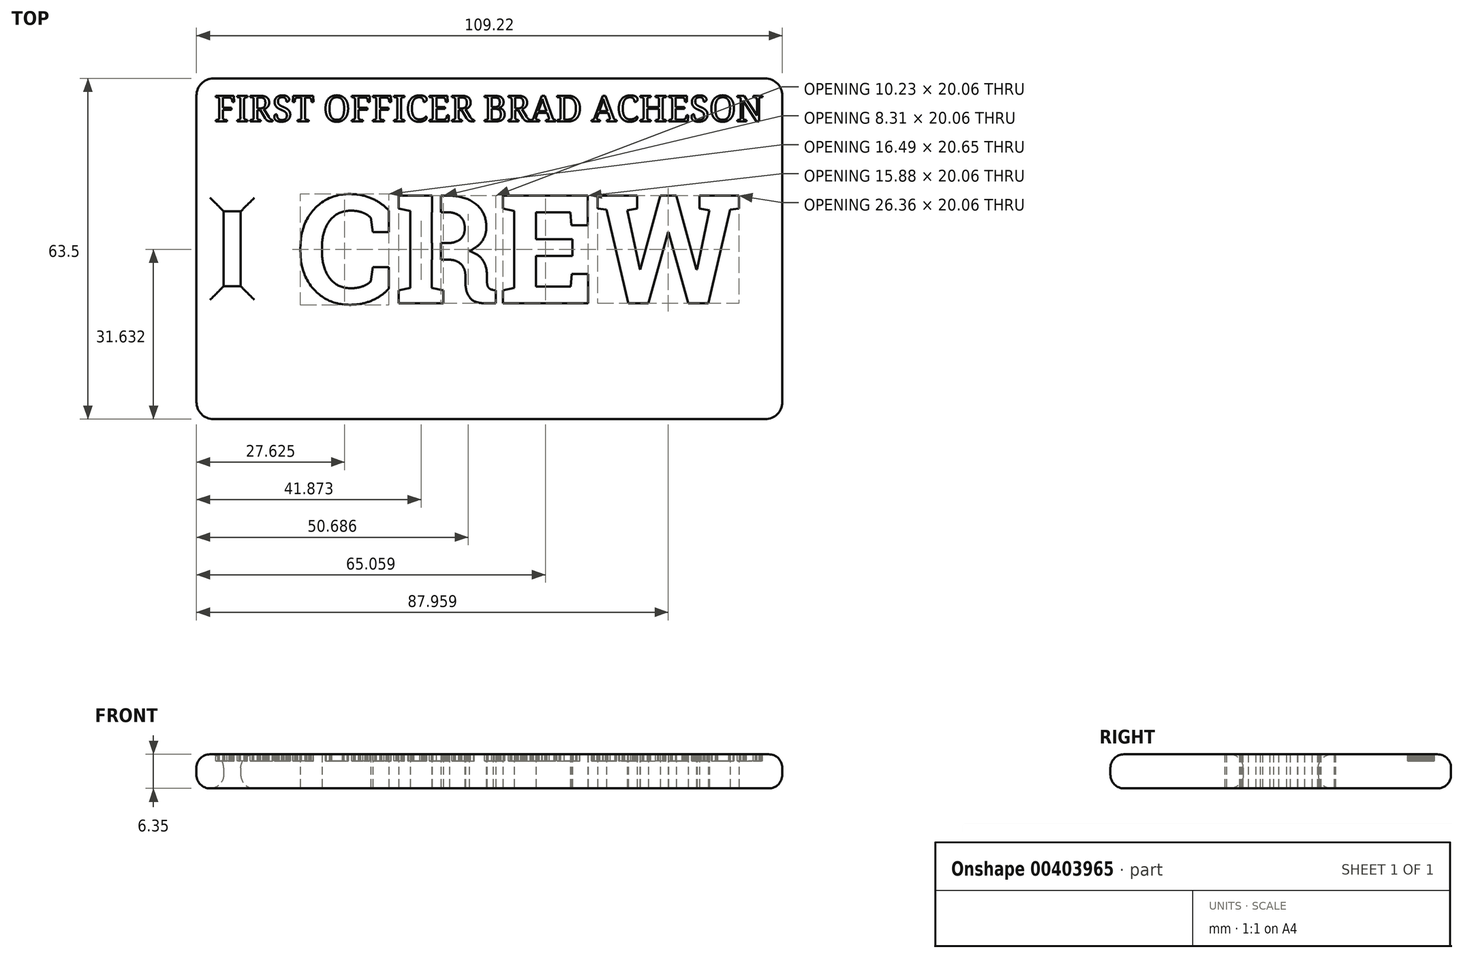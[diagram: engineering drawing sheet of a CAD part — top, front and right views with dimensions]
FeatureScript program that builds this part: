
annotation { "Feature Type Name" : "Feature", "Feature Type Description" : "" }
export const myFeature = defineFeature(function(context is Context, id is Id, definition is map)
    precondition{}
    {
        {
            var Q0;
            Q0=qCreatedBy(makeId("Top.planeOp"),FACE);
            var sketch = newSketch(context, id + "F0", { "sketchPlane" : qUnion([Q0])});
            skLineSegment(sketch, "E0.bottom", {"start": v(3.18, 0) * mm, "end": v(106.05, 0) * mm});
            skLineSegment(sketch, "E0.top", {"start": v(3.18, -63.5) * mm, "end": v(106.05, -63.5) * mm});
            skLineSegment(sketch, "E0.left", {"start": v(0, -3.18) * mm, "end": v(0, -60.33) * mm});
            skLineSegment(sketch, "E0.right", {"start": v(109.22, -3.18) * mm, "end": v(109.22, -60.33) * mm});
            skLineSegment(sketch, "E1.bottom", {"start": v(5.08, -24.77) * mm, "end": v(8.25, -24.77) * mm});
            skLineSegment(sketch, "E1.top", {"start": v(5.08, -38.74) * mm, "end": v(8.25, -38.74) * mm});
            skLineSegment(sketch, "E1.left", {"start": v(5.08, -24.76) * mm, "end": v(5.08, -38.73) * mm});
            skLineSegment(sketch, "E1.right", {"start": v(8.25, -24.76) * mm, "end": v(8.25, -38.73) * mm});
            skLineSegment(sketch, "E2", {"start": v(0, -31.75) * mm, "end": v(109.22, -31.75) * mm, "construction": true});
            skPoint(sketch, "E3.visualSharp", {"position": v(0, 0) * mm});
            skArc(sketch, "E3.filletArc", {"start": v(3.17, 0) * mm, "mid": v(0.93, -0.93) * mm, "end": v(0, -3.18) * mm});
            skPoint(sketch, "E4.visualSharp", {"position": v(109.22, 0) * mm});
            skArc(sketch, "E4.filletArc", {"start": v(109.22, -3.18) * mm, "mid": v(108.3, -0.93) * mm, "end": v(106.05, 0) * mm});
            skPoint(sketch, "E5.visualSharp", {"position": v(109.22, -63.5) * mm});
            skArc(sketch, "E5.filletArc", {"start": v(106.05, -63.5) * mm, "mid": v(108.3, -62.57) * mm, "end": v(109.22, -60.33) * mm});
            skPoint(sketch, "E6.visualSharp", {"position": v(0, -63.5) * mm});
            skArc(sketch, "E6.filletArc", {"start": v(0, -60.33) * mm, "mid": v(0.93, -62.57) * mm, "end": v(3.18, -63.5) * mm});
            skText(sketch, "E7", { "text": "CREW", "fontName": "RobotoSlab-Bold.ttf"});
            skLineSegment(sketch, "E8.bottom", {"start": v(45.57, -26.63) * mm, "end": v(43.9, -26.63) * mm});
            skLineSegment(sketch, "E8.top", {"start": v(45.57, -20.7) * mm, "end": v(43.9, -20.7) * mm});
            skLineSegment(sketch, "E8.left", {"start": v(45.57, -26.63) * mm, "end": v(45.57, -20.7) * mm});
            skLineSegment(sketch, "E8.right", {"start": v(43.9, -26.63) * mm, "end": v(43.9, -20.7) * mm});
            skLineSegment(sketch, "E9.bottom", {"start": v(45.57, -34.32) * mm, "end": v(43.9, -34.32) * mm});
            skLineSegment(sketch, "E9.top", {"start": v(45.57, -30.21) * mm, "end": v(43.9, -30.21) * mm});
            skLineSegment(sketch, "E9.left", {"start": v(45.57, -34.32) * mm, "end": v(45.57, -30.21) * mm});
            skLineSegment(sketch, "E9.right", {"start": v(43.9, -34.32) * mm, "end": v(43.9, -30.21) * mm});
            skLineSegment(sketch, "E10", {"start": v(43.9, -26.63) * mm, "end": v(43.9, -30.21) * mm, "construction": true});
            skLineSegment(sketch, "E11", {"start": v(45.57, -26.63) * mm, "end": v(45.57, -30.21) * mm, "construction": true});
            const initialGuessF0  = {"E7": [0.01866, -0.0419, 1, 0, 0.02032]};
            skSetInitialGuess(sketch, initialGuessF0);
            skSolve(sketch);
        }
        {
            var Q0;
            Q0=makeQuery(id+"F0.imprint","IMPRINT",FACE,{"disambiguationData":[TD([[makeQuery(id+"F0.imprint","IMPRINT",EDGE,{"derivedFrom":sQuery(id+"F0.wireOp",EDGE,"E0.bottom")}),-1.0]])]});
            var Q1;
            {var subQ0=sQuery(id+"F0.wireOp",EDGE,"E8.right");var subQ1=sQuery(id+"F0.wireOp",EDGE,"E7.sketch_text.stroke-52");var subQ2=makeQuery(id+"F0.imprint","INTERSECT",VERTEX,{"derivedFrom":[subQ1,subQ0]});Q1=makeQuery(id+"F0.imprint","IMPRINT",FACE,{"disambiguationData":[TD([[makeQuery(id+"F0.imprint","IMPRINT",EDGE,{"disambiguationData":[TD([[subQ2,-1.0]])],"derivedFrom":subQ1}),-1.0]])]});}
            var Q2;
            {var subQ5=sQuery(id+"F0.wireOp",EDGE,"E8.top");Q2=makeQuery(id+"F0.imprint","IMPRINT",FACE,{"disambiguationData":[TD([[makeQuery(id+"F0.imprint","IMPRINT",EDGE,{"derivedFrom":subQ5}),1.0]])]});}
            var Q3;
            {var subQ12=sQuery(id+"F0.wireOp",EDGE,"E7.sketch_text.stroke-54");Q3=makeQuery(id+"F0.imprint","IMPRINT",FACE,{"disambiguationData":[TD([[makeQuery(id+"F0.imprint","IMPRINT",EDGE,{"derivedFrom":subQ12}),1.0]])]});}
            var Q4;
            {var subQ5=sQuery(id+"F0.wireOp",EDGE,"E8.bottom");Q4=makeQuery(id+"F0.imprint","IMPRINT",FACE,{"disambiguationData":[TD([[makeQuery(id+"F0.imprint","IMPRINT",EDGE,{"derivedFrom":subQ5}),-1.0]])]});}
            var Q5;
            {var subQ5=sQuery(id+"F0.wireOp",EDGE,"E9.top");Q5=makeQuery(id+"F0.imprint","IMPRINT",FACE,{"disambiguationData":[TD([[makeQuery(id+"F0.imprint","IMPRINT",EDGE,{"derivedFrom":subQ5}),1.0]])]});}
            var Q6;
            {var subQ5=sQuery(id+"F0.wireOp",EDGE,"E9.bottom");Q6=makeQuery(id+"F0.imprint","IMPRINT",FACE,{"disambiguationData":[TD([[makeQuery(id+"F0.imprint","IMPRINT",EDGE,{"derivedFrom":subQ5}),-1.0]])]});}
            var Q7;
            {var subQ0=sQuery(id+"F0.wireOp",EDGE,"E9.left");var subQ1=sQuery(id+"F0.wireOp",EDGE,"E7.sketch_text.stroke-41");var subQ2=makeQuery(id+"F0.imprint","INTERSECT",VERTEX,{"derivedFrom":[subQ1,subQ0]});Q7=makeQuery(id+"F0.imprint","IMPRINT",FACE,{"disambiguationData":[TD([[makeQuery(id+"F0.imprint","IMPRINT",EDGE,{"disambiguationData":[TD([[subQ2,-1.0]])],"derivedFrom":subQ1}),-1.0]])]});}
            extrude(context, id + "F1", {"entities" : qUnion([Q0, Q1, Q2, Q3, Q4, Q5, Q6, Q7]), "depth" : 6.35 * mm});
        }
        {
            var Q0;
            Q0=makeQuery(id+"F1.opExtrude","CAP_FACE",FACE,{"disambiguationData":[OSD([sQuery(id+"F0.wireOp",EDGE,"E0.bottom"),sQuery(id+"F0.wireOp",EDGE,"E0.top"),sQuery(id+"F0.wireOp",EDGE,"E0.left"),sQuery(id+"F0.wireOp",EDGE,"E0.right"),sQuery(id+"F0.wireOp",EDGE,"E1.bottom"),sQuery(id+"F0.wireOp",EDGE,"E1.top"),sQuery(id+"F0.wireOp",EDGE,"E1.left"),sQuery(id+"F0.wireOp",EDGE,"E1.right"),sQuery(id+"F0.wireOp",EDGE,"E3.filletArc"),sQuery(id+"F0.wireOp",EDGE,"E4.filletArc"),sQuery(id+"F0.wireOp",EDGE,"E5.filletArc"),sQuery(id+"F0.wireOp",EDGE,"E6.filletArc"),sQuery(id+"F0.wireOp",EDGE,"E7.sketch_text.stroke-0"),sQuery(id+"F0.wireOp",EDGE,"E7.sketch_text.stroke-1"),sQuery(id+"F0.wireOp",EDGE,"E7.sketch_text.stroke-2"),sQuery(id+"F0.wireOp",EDGE,"E7.sketch_text.stroke-3"),sQuery(id+"F0.wireOp",EDGE,"E7.sketch_text.stroke-4"),sQuery(id+"F0.wireOp",EDGE,"E7.sketch_text.stroke-5"),sQuery(id+"F0.wireOp",EDGE,"E7.sketch_text.stroke-6"),sQuery(id+"F0.wireOp",EDGE,"E7.sketch_text.stroke-7"),sQuery(id+"F0.wireOp",EDGE,"E7.sketch_text.stroke-8"),sQuery(id+"F0.wireOp",EDGE,"E7.sketch_text.stroke-9"),sQuery(id+"F0.wireOp",EDGE,"E7.sketch_text.stroke-10"),sQuery(id+"F0.wireOp",EDGE,"E7.sketch_text.stroke-11"),sQuery(id+"F0.wireOp",EDGE,"E7.sketch_text.stroke-12"),sQuery(id+"F0.wireOp",EDGE,"E7.sketch_text.stroke-13"),sQuery(id+"F0.wireOp",EDGE,"E7.sketch_text.stroke-14"),sQuery(id+"F0.wireOp",EDGE,"E7.sketch_text.stroke-15"),sQuery(id+"F0.wireOp",EDGE,"E7.sketch_text.stroke-16"),sQuery(id+"F0.wireOp",EDGE,"E7.sketch_text.stroke-17"),sQuery(id+"F0.wireOp",EDGE,"E7.sketch_text.stroke-18"),sQuery(id+"F0.wireOp",EDGE,"E7.sketch_text.stroke-19"),sQuery(id+"F0.wireOp",EDGE,"E7.sketch_text.stroke-20"),sQuery(id+"F0.wireOp",EDGE,"E7.sketch_text.stroke-21"),sQuery(id+"F0.wireOp",EDGE,"E7.sketch_text.stroke-22"),sQuery(id+"F0.wireOp",EDGE,"E7.sketch_text.stroke-23"),sQuery(id+"F0.wireOp",EDGE,"E7.sketch_text.stroke-24"),sQuery(id+"F0.wireOp",EDGE,"E7.sketch_text.stroke-25"),sQuery(id+"F0.wireOp",EDGE,"E7.sketch_text.stroke-26"),sQuery(id+"F0.wireOp",EDGE,"E7.sketch_text.stroke-27"),sQuery(id+"F0.wireOp",EDGE,"E7.sketch_text.stroke-28"),sQuery(id+"F0.wireOp",EDGE,"E7.sketch_text.stroke-29"),sQuery(id+"F0.wireOp",EDGE,"E7.sketch_text.stroke-30"),sQuery(id+"F0.wireOp",EDGE,"E7.sketch_text.stroke-31"),sQuery(id+"F0.wireOp",EDGE,"E7.sketch_text.stroke-32"),sQuery(id+"F0.wireOp",EDGE,"E7.sketch_text.stroke-33"),sQuery(id+"F0.wireOp",EDGE,"E7.sketch_text.stroke-34"),sQuery(id+"F0.wireOp",EDGE,"E7.sketch_text.stroke-35"),sQuery(id+"F0.wireOp",EDGE,"E7.sketch_text.stroke-36"),sQuery(id+"F0.wireOp",EDGE,"E7.sketch_text.stroke-37"),sQuery(id+"F0.wireOp",EDGE,"E7.sketch_text.stroke-38"),sQuery(id+"F0.wireOp",EDGE,"E7.sketch_text.stroke-39"),sQuery(id+"F0.wireOp",EDGE,"E7.sketch_text.stroke-40"),sQuery(id+"F0.wireOp",EDGE,"E7.sketch_text.stroke-41"),sQuery(id+"F0.wireOp",EDGE,"E7.sketch_text.stroke-42"),sQuery(id+"F0.wireOp",EDGE,"E7.sketch_text.stroke-43"),sQuery(id+"F0.wireOp",EDGE,"E7.sketch_text.stroke-44"),sQuery(id+"F0.wireOp",EDGE,"E7.sketch_text.stroke-45"),sQuery(id+"F0.wireOp",EDGE,"E7.sketch_text.stroke-46"),sQuery(id+"F0.wireOp",EDGE,"E7.sketch_text.stroke-47"),sQuery(id+"F0.wireOp",EDGE,"E7.sketch_text.stroke-48"),sQuery(id+"F0.wireOp",EDGE,"E7.sketch_text.stroke-49"),sQuery(id+"F0.wireOp",EDGE,"E7.sketch_text.stroke-50"),sQuery(id+"F0.wireOp",EDGE,"E7.sketch_text.stroke-51"),sQuery(id+"F0.wireOp",EDGE,"E7.sketch_text.stroke-52"),sQuery(id+"F0.wireOp",EDGE,"E7.sketch_text.stroke-53"),sQuery(id+"F0.wireOp",EDGE,"E7.sketch_text.stroke-54"),sQuery(id+"F0.wireOp",EDGE,"E7.sketch_text.stroke-55"),sQuery(id+"F0.wireOp",EDGE,"E7.sketch_text.stroke-56"),sQuery(id+"F0.wireOp",EDGE,"E7.sketch_text.stroke-57"),sQuery(id+"F0.wireOp",EDGE,"E7.sketch_text.stroke-58"),sQuery(id+"F0.wireOp",EDGE,"E7.sketch_text.stroke-59"),sQuery(id+"F0.wireOp",EDGE,"E7.sketch_text.stroke-60"),sQuery(id+"F0.wireOp",EDGE,"E7.sketch_text.stroke-61"),sQuery(id+"F0.wireOp",EDGE,"E7.sketch_text.stroke-62"),sQuery(id+"F0.wireOp",EDGE,"E7.sketch_text.stroke-63"),sQuery(id+"F0.wireOp",EDGE,"E7.sketch_text.stroke-64"),sQuery(id+"F0.wireOp",EDGE,"E7.sketch_text.stroke-65"),sQuery(id+"F0.wireOp",EDGE,"E7.sketch_text.stroke-66"),sQuery(id+"F0.wireOp",EDGE,"E7.sketch_text.stroke-67"),sQuery(id+"F0.wireOp",EDGE,"E7.sketch_text.stroke-68"),sQuery(id+"F0.wireOp",EDGE,"E7.sketch_text.stroke-69"),sQuery(id+"F0.wireOp",EDGE,"E7.sketch_text.stroke-70"),sQuery(id+"F0.wireOp",EDGE,"E7.sketch_text.stroke-71"),sQuery(id+"F0.wireOp",EDGE,"E7.sketch_text.stroke-72"),sQuery(id+"F0.wireOp",EDGE,"E7.sketch_text.stroke-73"),sQuery(id+"F0.wireOp",EDGE,"E7.sketch_text.stroke-74"),sQuery(id+"F0.wireOp",EDGE,"E7.sketch_text.stroke-75"),sQuery(id+"F0.wireOp",EDGE,"E7.sketch_text.stroke-76"),sQuery(id+"F0.wireOp",EDGE,"E7.sketch_text.stroke-77"),sQuery(id+"F0.wireOp",EDGE,"E7.sketch_text.stroke-78"),sQuery(id+"F0.wireOp",EDGE,"E7.sketch_text.stroke-79"),sQuery(id+"F0.wireOp",EDGE,"E7.sketch_text.stroke-80"),sQuery(id+"F0.wireOp",EDGE,"E7.sketch_text.stroke-81"),sQuery(id+"F0.wireOp",EDGE,"E7.sketch_text.stroke-82"),sQuery(id+"F0.wireOp",EDGE,"E7.sketch_text.stroke-83"),sQuery(id+"F0.wireOp",EDGE,"E7.sketch_text.stroke-84"),sQuery(id+"F0.wireOp",EDGE,"E7.sketch_text.stroke-85"),sQuery(id+"F0.wireOp",EDGE,"E7.sketch_text.stroke-86"),sQuery(id+"F0.wireOp",EDGE,"E7.sketch_text.stroke-87"),sQuery(id+"F0.wireOp",EDGE,"E7.sketch_text.stroke-88"),sQuery(id+"F0.wireOp",EDGE,"E7.sketch_text.stroke-89"),sQuery(id+"F0.wireOp",EDGE,"E7.sketch_text.stroke-90"),sQuery(id+"F0.wireOp",EDGE,"E7.sketch_text.stroke-91"),sQuery(id+"F0.wireOp",EDGE,"E7.sketch_text.stroke-92"),sQuery(id+"F0.wireOp",EDGE,"E7.sketch_text.stroke-93"),sQuery(id+"F0.wireOp",EDGE,"E7.sketch_text.stroke-94"),sQuery(id+"F0.wireOp",EDGE,"E7.sketch_text.stroke-95"),sQuery(id+"F0.wireOp",EDGE,"E7.sketch_text.stroke-96"),sQuery(id+"F0.wireOp",EDGE,"E7.sketch_text.stroke-97"),sQuery(id+"F0.wireOp",EDGE,"E7.sketch_text.stroke-98"),sQuery(id+"F0.wireOp",EDGE,"E7.sketch_text.stroke-99"),sQuery(id+"F0.wireOp",EDGE,"E7.sketch_text.stroke-100"),sQuery(id+"F0.wireOp",EDGE,"E7.sketch_text.stroke-101"),sQuery(id+"F0.wireOp",EDGE,"E7.sketch_text.stroke-102"),sQuery(id+"F0.wireOp",EDGE,"E7.sketch_text.stroke-103"),sQuery(id+"F0.wireOp",EDGE,"E7.sketch_text.stroke-104"),sQuery(id+"F0.wireOp",EDGE,"E8.left"),sQuery(id+"F0.wireOp",EDGE,"E8.right"),sQuery(id+"F0.wireOp",EDGE,"E9.left"),sQuery(id+"F0.wireOp",EDGE,"E9.right")])],"isStart":false});
            var sketch = newSketch(context, id + "F2", { "sketchPlane" : qUnion([Q0])});
            skText(sketch, "E12", { "text": "FIRST OFFICER BRAD ACHESON", "fontName": "NotoSerif-Regular.ttf"});
            skLineSegment(sketch, "E13", {"start": v(54.61, 0) * mm, "end": v(54.61, -3.18) * mm, "construction": true});
            const initialGuessF2  = {"E12": [0.00336, -0.008, 1, 0, 0.00483]};
            skSetInitialGuess(sketch, initialGuessF2);
            skSolve(sketch);
        }
        {
            var Q0;
            Q0 = qSketchRegion(id + "F2", true);
            extrude(context, id + "F3", {"entities" : qUnion([Q0]), "operationType" : NewBodyOperationType.REMOVE, "oppositeDirection" : true, "depth" : 1.27 * mm});
        }
        {
            var Q0;
            Q0=makeQuery(id+"F1.opExtrude","CAP_EDGE",EDGE,{"disambiguationData":[OSD([sQuery(id+"F0.wireOp",EDGE,"E0.bottom")])],"isStart":false});
            var Q1;
            Q1=makeQuery(id+"F1.opExtrude","CAP_EDGE",EDGE,{"disambiguationData":[OSD([sQuery(id+"F0.wireOp",EDGE,"E0.bottom")])],"isStart":true});
            var Q2;
            Q2=makeQuery(id+"F1.opExtrude","CAP_EDGE",EDGE,{"disambiguationData":[OSD([sQuery(id+"F0.wireOp",EDGE,"E1.left")])],"isStart":false});
            var Q3;
            Q3=makeQuery(id+"F1.opExtrude","CAP_EDGE",EDGE,{"disambiguationData":[OSD([sQuery(id+"F0.wireOp",EDGE,"E1.bottom")])],"isStart":false});
            var Q4;
            Q4=makeQuery(id+"F1.opExtrude","CAP_EDGE",EDGE,{"disambiguationData":[OSD([sQuery(id+"F0.wireOp",EDGE,"E1.right")])],"isStart":false});
            var Q5;
            Q5=makeQuery(id+"F1.opExtrude","CAP_EDGE",EDGE,{"disambiguationData":[OSD([sQuery(id+"F0.wireOp",EDGE,"E1.top")])],"isStart":false});
            var Q6;
            Q6=makeQuery(id+"F1.opExtrude","CAP_EDGE",EDGE,{"disambiguationData":[OSD([sQuery(id+"F0.wireOp",EDGE,"E1.right")])],"isStart":true});
            var Q7;
            Q7=makeQuery(id+"F1.opExtrude","CAP_EDGE",EDGE,{"disambiguationData":[OSD([sQuery(id+"F0.wireOp",EDGE,"E1.bottom")])],"isStart":true});
            var Q8;
            Q8=makeQuery(id+"F1.opExtrude","CAP_EDGE",EDGE,{"disambiguationData":[OSD([sQuery(id+"F0.wireOp",EDGE,"E1.top")])],"isStart":true});
            var Q9;
            Q9=makeQuery(id+"F1.opExtrude","CAP_EDGE",EDGE,{"disambiguationData":[OSD([sQuery(id+"F0.wireOp",EDGE,"E1.left")])],"isStart":true});
            fillet(context, id + "F4", {"entities" : qUnion([Q0, Q1, Q2, Q3, Q4, Q5, Q6, Q7, Q8, Q9]), "radius" : 2.54 * mm, "tangentPropagation" : true, "allowEdgeOverflow" : false});
        }
    });
